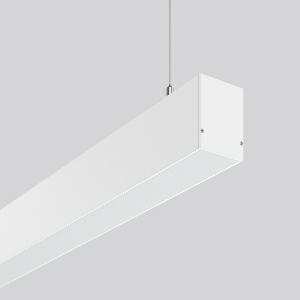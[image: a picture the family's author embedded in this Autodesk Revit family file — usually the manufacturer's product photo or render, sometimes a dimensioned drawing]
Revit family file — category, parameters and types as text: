
# Revit family: less_is_more_50_312313_002_1_76_5630
name_source: partatom
category: Lighting Fixtures
units: mm (PartAtom-declared; Revit-internal decimal feet)

## family parameters
Cut with Voids When Loaded = No
Host = Face
Light Source = No
Part Type = Normal
Room Calculation Point = No
Round Connector Dimension = Use Diameter
Shared = No

## types (1)
- LESS IS MORE 50 (1 x LED Modul 840, 4050 lm, 4000)
    Apparent Load = 34 VA
    CIE Flux Codes = 48 79 95 100 100
    Color Rendering = 80
    Color Temperature = 4000
    Default Elevation = 1800 mm
    Description = Series: LESS IS MORE 50
Linear pendant luminaire for aesthetically sophisticated lighting. Housing: extruded aluminium profile, powder-coated. End cap aluminium powder-coated. Canopy made of aluminium, powder-coated. Diffuser made of non-yellowing plastic (PMMA), opal. Direct light emission. Suitable for pendant. 2-point steel cable suspension freely positionable and infinitely height-adjustable. Special lengths available on request. LED unit with integrated converter interchangeable and removable. Suitable for through-wiring. With sensors or as a safety luminaire on request. 
Colour: traffic white, matt (RAL 9016)
Length: 1407 mm
Width: 57 mm
Height: 75 mm
Suspension length: 2000 mm
Lamp: LED
Socket: without socket
Colour temperature: 4000K
Colour rendering index (CRI): 80
System power: 34 W
Rated luminous flux: 4050 lm
Luminous efficiency: 119 lm/W
Control gear: Converter, dimmable, DALI
Protection class: I
Type of protection: IP 20
    Height = 75 mm
    Lamp = 1 x LED Modul 840
    Lamp Light Flux = 4050 lm
    Lamp count = 1
    Length = 1407 mm
    Lifetime = 50000 h
    Luminous efficacy = 119 lm/W
    Manufacturer = RZB
    ModVariant = No
    Model = 312313.002.1.76
    Mounting Place = Ceiling
    Mounting Type = Pendant
    Number of Poles = 1
    OnlyDefault = Yes
    Power Factor = 1
    Product Name = LESS IS MORE 50
    Product group = Pendant LED linear luminaires
    ProductGroupID = 907
    Protection Class = Protection class I
    Protection Degree = IP 20
    RLX_Detail_Level = 1
    RLX_Emergency_Light_Flux = 0 lm
    RLX_Emergency_Type = 0
    RLX_Emergency_Type_DB = No
    RlxData = <blob elided: 20589 chars, md5=634fa04a>
    Socket = socket
    Standby Power = 0 W
    System Light Flux = 4050 lm
    System Power = 34 W
    Type Comments = Product without accessories
    Type Image = 312318.002.jpg
    URL = http://relux.com
    VarID = ---
    Voltage = 230 V
    Voltage Range = 220-240 V
    Weight = 0.00 kg
    Width = 57 mm

## geometry (parser evidence)
native form markers: Blend x4, Sweep x14
no freeform markers — native parametric forms only
